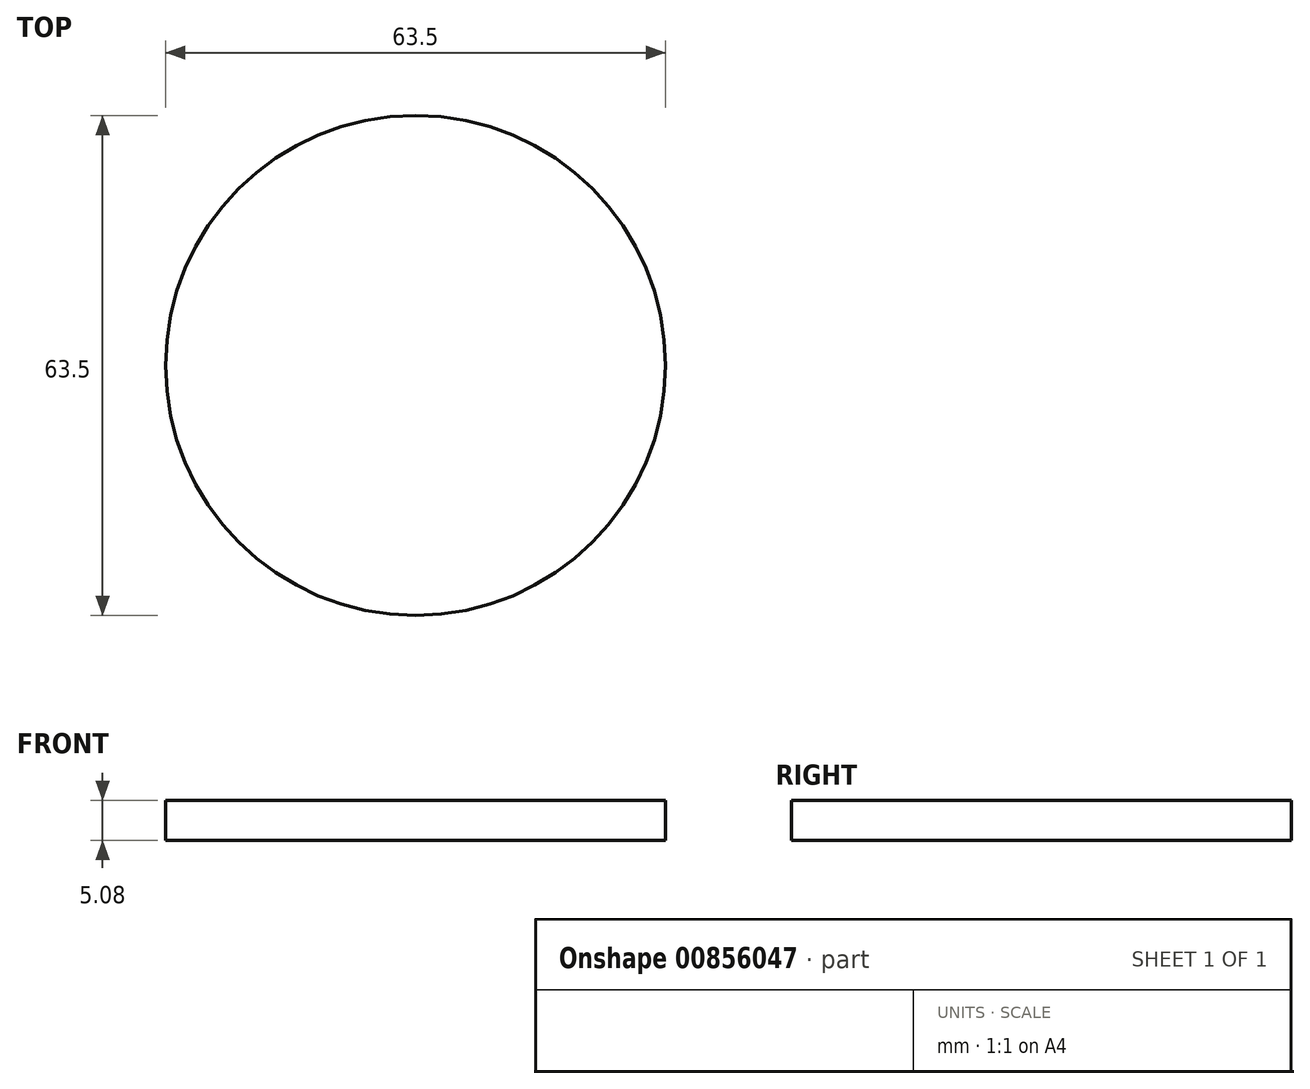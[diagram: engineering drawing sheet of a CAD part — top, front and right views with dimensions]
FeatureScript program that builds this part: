
annotation { "Feature Type Name" : "Feature", "Feature Type Description" : "" }
export const myFeature = defineFeature(function(context is Context, id is Id, definition is map)
    precondition{}
    {
        {
            var Q0;
            Q0=qCreatedBy(makeId("Top.planeOp"),FACE);
            var sketch = newSketch(context, id + "F0", { "sketchPlane" : qUnion([Q0])});
            skCircle(sketch, "E0", {"center": v(0, 0) * mm, "radius": 31.75 * mm});
            skSolve(sketch);
        }
        {
            var Q0;
            Q0=makeQuery(id+"F0.imprint","IMPRINT",FACE,{"disambiguationData":[TD([[makeQuery(id+"F0.imprint","IMPRINT",EDGE,{"derivedFrom":sQuery(id+"F0.wireOp",EDGE,"E0")}),1.0]])]});
            extrude(context, id + "F1", {"entities" : qUnion([Q0]), "depth" : 5.08 * mm, "offsetDistance" : 25.4 * mm});
        }
    });
